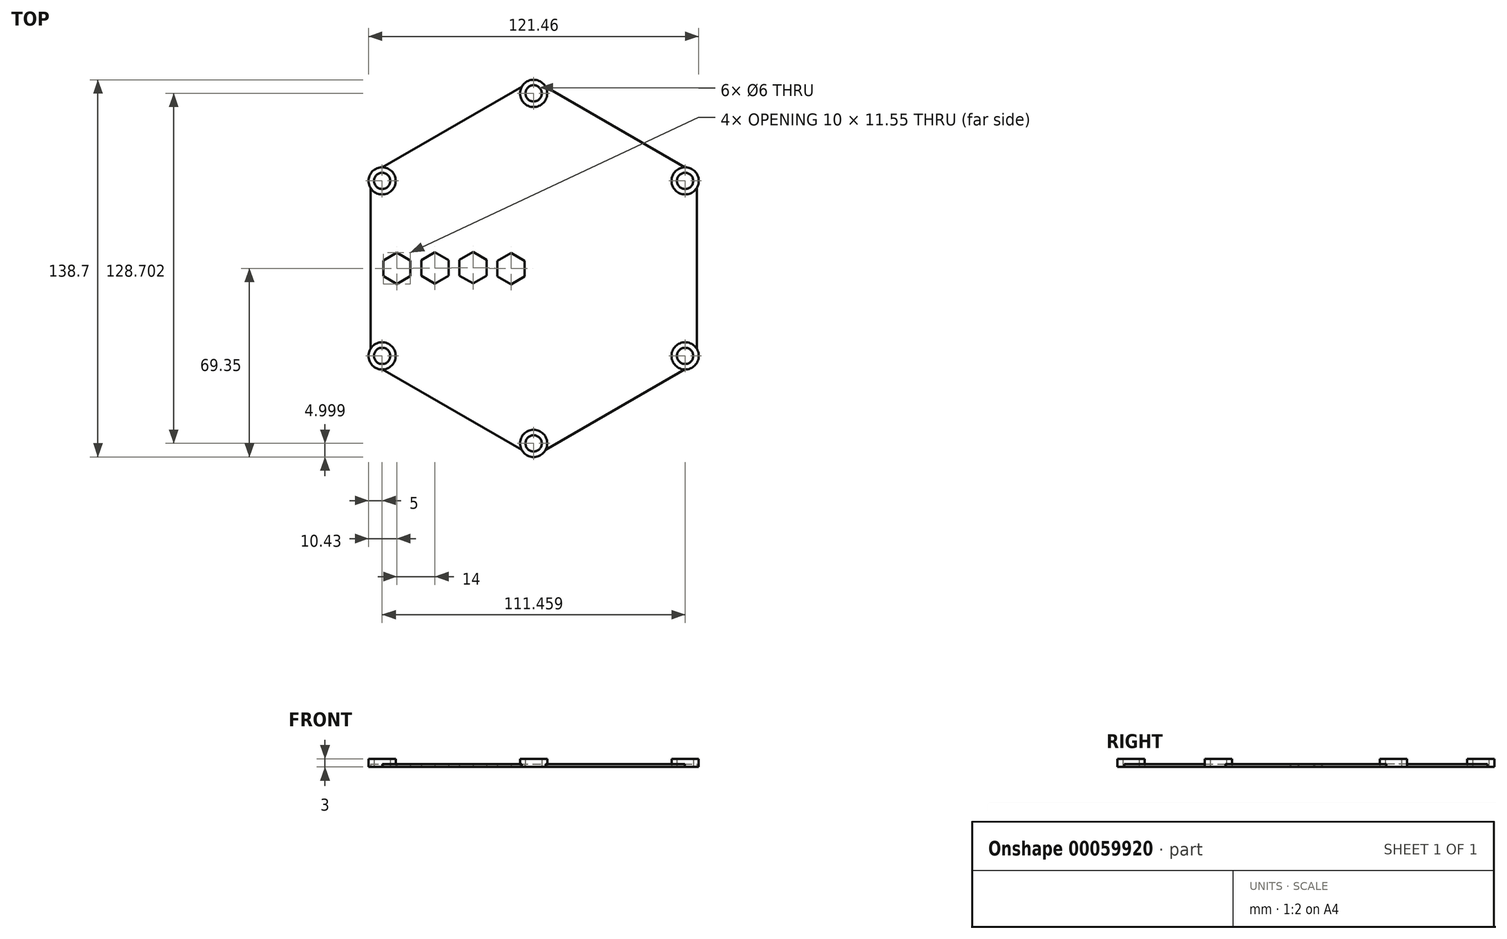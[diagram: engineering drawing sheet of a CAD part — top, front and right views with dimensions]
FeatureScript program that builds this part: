
annotation { "Feature Type Name" : "Feature", "Feature Type Description" : "" }
export const myFeature = defineFeature(function(context is Context, id is Id, definition is map)
    precondition{}
    {
        {
            var Q0;
            Q0=qCreatedBy(makeId("Top.planeOp"),FACE);
            var sketch = newSketch(context, id + "F0", { "sketchPlane" : qUnion([Q0])});
            skCircle(sketch, "E0.cCircle", {"center": v(0, 0) * mm, "radius": 60 * mm, "construction": true});
            skLineSegment(sketch, "E0.0", {"start": v(60, 29.57) * mm, "end": v(60, -29.57) * mm});
            skLineSegment(sketch, "E0.1", {"start": v(55.61, -37.17) * mm, "end": v(4.39, -66.75) * mm});
            skLineSegment(sketch, "E0.2", {"start": v(-4.39, -66.75) * mm, "end": v(-55.61, -37.17) * mm});
            skLineSegment(sketch, "E0.3", {"start": v(-60, -29.57) * mm, "end": v(-60, 29.57) * mm});
            skLineSegment(sketch, "E0.4", {"start": v(-55.61, 37.17) * mm, "end": v(-4.39, 66.75) * mm});
            skLineSegment(sketch, "E0.5", {"start": v(4.39, 66.75) * mm, "end": v(55.61, 37.17) * mm});
            skPoint(sketch, "E0.0.midPoint", {"position": v(60, 0) * mm});
            skCircle(sketch, "E1", {"center": v(0, 64.35) * mm, "radius": 5 * mm});
            skCircle(sketch, "E2.0", {"center": v(0, 64.35) * mm, "radius": 3 * mm});
            skCircle(sketch, "E3.1.0", {"center": v(55.73, 32.18) * mm, "radius": 3 * mm});
            skCircle(sketch, "E3.1.1", {"center": v(55.73, 32.18) * mm, "radius": 5 * mm});
            skCircle(sketch, "E3.2.0", {"center": v(55.73, -32.18) * mm, "radius": 3 * mm});
            skCircle(sketch, "E3.2.1", {"center": v(55.73, -32.18) * mm, "radius": 5 * mm});
            skCircle(sketch, "E3.3.0", {"center": v(0, -64.35) * mm, "radius": 3 * mm});
            skCircle(sketch, "E3.3.1", {"center": v(0, -64.35) * mm, "radius": 5 * mm});
            skCircle(sketch, "E3.4.0", {"center": v(-55.73, -32.18) * mm, "radius": 3 * mm});
            skCircle(sketch, "E3.4.1", {"center": v(-55.73, -32.18) * mm, "radius": 5 * mm});
            skCircle(sketch, "E3.5.0", {"center": v(-55.73, 32.18) * mm, "radius": 3 * mm});
            skCircle(sketch, "E3.5.1", {"center": v(-55.73, 32.18) * mm, "radius": 5 * mm});
            skLineSegment(sketch, "E3.anchor1", {"start": v(0, 0) * mm, "end": v(0, 64.35) * mm, "construction": true});
            skLineSegment(sketch, "E3.anchor2", {"start": v(0, 0) * mm, "end": v(-55.73, 32.18) * mm, "construction": true});
            skPoint(sketch, "E4.orphan", {"position": v(-60, 34.64) * mm});
            skPoint(sketch, "E5.orphan", {"position": v(-60, -34.64) * mm});
            skPoint(sketch, "E6.orphan", {"position": v(60, -34.64) * mm});
            skPoint(sketch, "E7.orphan", {"position": v(60, 34.64) * mm});
            skPoint(sketch, "E8.orphan", {"position": v(0, 69.28) * mm});
            skPoint(sketch, "E9.orphan", {"position": v(0, -69.28) * mm});
            skCircle(sketch, "E10.cCircle", {"center": v(-50.3, 0) * mm, "radius": 5 * mm, "construction": true});
            skPoint(sketch, "E10.cCircle.centerSnap0", {"position": v(-60, 0) * mm});
            skPoint(sketch, "E10.cCircle.perimeterSnap0", {"position": v(-60, 0) * mm});
            skLineSegment(sketch, "E10.0", {"start": v(-45.3, 2.89) * mm, "end": v(-45.3, -2.89) * mm});
            skLineSegment(sketch, "E10.1", {"start": v(-45.3, -2.89) * mm, "end": v(-50.3, -5.77) * mm});
            skLineSegment(sketch, "E10.2", {"start": v(-50.3, -5.77) * mm, "end": v(-55.3, -2.89) * mm});
            skLineSegment(sketch, "E10.3", {"start": v(-55.3, -2.89) * mm, "end": v(-55.3, 2.89) * mm});
            skLineSegment(sketch, "E10.4", {"start": v(-55.3, 2.89) * mm, "end": v(-50.3, 5.77) * mm});
            skLineSegment(sketch, "E10.5", {"start": v(-50.3, 5.77) * mm, "end": v(-45.3, 2.89) * mm});
            skPoint(sketch, "E10.0.midPoint", {"position": v(-45.3, 0) * mm});
            skPoint(sketch, "E10.0.midPoint.positionSnap0", {"position": v(-60, 0) * mm});
            skLineSegment(sketch, "E11.3", {"start": v(-41.3, -2.76) * mm, "end": v(-41.3, 3.02) * mm});
            skLineSegment(sketch, "E11.5", {"start": v(-36.3, 5.9) * mm, "end": v(-31.3, 3.02) * mm});
            skLineSegment(sketch, "E11.1", {"start": v(-31.3, -2.76) * mm, "end": v(-36.3, -5.64) * mm});
            skLineSegment(sketch, "E11.2", {"start": v(-36.3, -5.64) * mm, "end": v(-41.3, -2.76) * mm});
            skCircle(sketch, "E11.cCircle", {"center": v(-36.3, 0.13) * mm, "radius": 5 * mm, "construction": true});
            skPoint(sketch, "E11.0.midPoint", {"position": v(-31.3, 0.13) * mm});
            skLineSegment(sketch, "E11.4", {"start": v(-41.3, 3.02) * mm, "end": v(-36.3, 5.9) * mm});
            skLineSegment(sketch, "E11.0", {"start": v(-31.3, 3.02) * mm, "end": v(-31.3, -2.76) * mm});
            skLineSegment(sketch, "E12.3", {"start": v(-27.3, -2.65) * mm, "end": v(-27.3, 3.12) * mm});
            skLineSegment(sketch, "E12.5", {"start": v(-22.3, 6) * mm, "end": v(-17.3, 3.12) * mm});
            skLineSegment(sketch, "E12.1", {"start": v(-17.3, -2.65) * mm, "end": v(-22.3, -5.54) * mm});
            skLineSegment(sketch, "E12.2", {"start": v(-22.3, -5.54) * mm, "end": v(-27.3, -2.65) * mm});
            skCircle(sketch, "E12.cCircle", {"center": v(-22.3, 0.23) * mm, "radius": 5 * mm, "construction": true});
            skPoint(sketch, "E12.0.midPoint", {"position": v(-17.3, 0.23) * mm});
            skLineSegment(sketch, "E12.4", {"start": v(-27.3, 3.12) * mm, "end": v(-22.3, 6) * mm});
            skLineSegment(sketch, "E12.0", {"start": v(-17.3, 3.12) * mm, "end": v(-17.3, -2.65) * mm});
            skLineSegment(sketch, "E13.3", {"start": v(-13.3, -2.96) * mm, "end": v(-13.3, 2.8) * mm});
            skLineSegment(sketch, "E13.5", {"start": v(-8.3, 5.7) * mm, "end": v(-3.3, 2.8) * mm});
            skLineSegment(sketch, "E13.1", {"start": v(-3.3, -2.96) * mm, "end": v(-8.3, -5.85) * mm});
            skLineSegment(sketch, "E13.2", {"start": v(-8.3, -5.85) * mm, "end": v(-13.3, -2.96) * mm});
            skCircle(sketch, "E13.cCircle", {"center": v(-8.3, -0.08) * mm, "radius": 5 * mm, "construction": true});
            skPoint(sketch, "E13.0.midPoint", {"position": v(-3.3, -0.08) * mm});
            skLineSegment(sketch, "E13.4", {"start": v(-13.3, 2.8) * mm, "end": v(-8.3, 5.7) * mm});
            skLineSegment(sketch, "E13.0", {"start": v(-3.3, 2.8) * mm, "end": v(-3.3, -2.96) * mm});
            skSolve(sketch);
        }
        {
            var Q0;
            {var subQ1=sQuery(id+"F0.wireOp",EDGE,"E0.0");var subQ9=sQuery(id+"F0.wireOp",EDGE,"E3.1.1");var subQ10=makeQuery(id+"F0.imprint","INTERSECT",VERTEX,{"derivedFrom":[subQ1,subQ9]});Q0=makeQuery(id+"F0.imprint","IMPRINT",FACE,{"disambiguationData":[TD([[makeQuery(id+"F0.imprint","IMPRINT",EDGE,{"disambiguationData":[TD([[subQ10,-1.0]])],"derivedFrom":subQ1}),-1.0]])]});}
            extrude(context, id + "F1", {"entities" : qUnion([Q0]), "depth" : 1 * mm});
        }
        {
            var Q0;
            Q0=makeQuery(id+"F0.imprint","IMPRINT",FACE,{"disambiguationData":[TD([[makeQuery(id+"F0.imprint","IMPRINT",EDGE,{"derivedFrom":sQuery(id+"F0.wireOp",EDGE,"E3.5.0")}),-1.0]])]});
            var Q1;
            Q1=makeQuery(id+"F0.imprint","IMPRINT",FACE,{"disambiguationData":[TD([[makeQuery(id+"F0.imprint","IMPRINT",EDGE,{"derivedFrom":sQuery(id+"F0.wireOp",EDGE,"E2.0")}),-1.0]])]});
            var Q2;
            Q2=makeQuery(id+"F0.imprint","IMPRINT",FACE,{"disambiguationData":[TD([[makeQuery(id+"F0.imprint","IMPRINT",EDGE,{"derivedFrom":sQuery(id+"F0.wireOp",EDGE,"E3.1.0")}),-1.0]])]});
            var Q3;
            Q3=makeQuery(id+"F0.imprint","IMPRINT",FACE,{"disambiguationData":[TD([[makeQuery(id+"F0.imprint","IMPRINT",EDGE,{"derivedFrom":sQuery(id+"F0.wireOp",EDGE,"E3.2.0")}),-1.0]])]});
            var Q4;
            Q4=makeQuery(id+"F0.imprint","IMPRINT",FACE,{"disambiguationData":[TD([[makeQuery(id+"F0.imprint","IMPRINT",EDGE,{"derivedFrom":sQuery(id+"F0.wireOp",EDGE,"E3.3.0")}),-1.0]])]});
            var Q5;
            Q5=makeQuery(id+"F0.imprint","IMPRINT",FACE,{"disambiguationData":[TD([[makeQuery(id+"F0.imprint","IMPRINT",EDGE,{"derivedFrom":sQuery(id+"F0.wireOp",EDGE,"E3.4.0")}),-1.0]])]});
            extrude(context, id + "F2", {"entities" : qUnion([Q0, Q1, Q2, Q3, Q4, Q5]), "depth" : 3 * mm});
        }
    });
